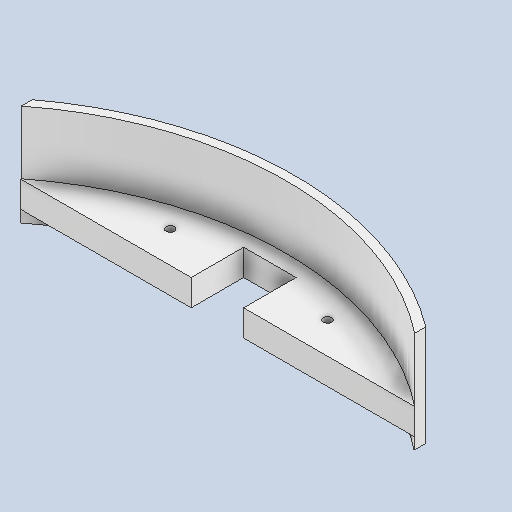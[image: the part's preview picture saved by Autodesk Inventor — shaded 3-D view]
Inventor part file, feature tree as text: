
AUTODESK INVENTOR PART (.ipt)
format: ipt  version: 2023 (Build 270158000, 158)  size: 375,296 bytes
history: native  units: mm
features: sketch x14, extrude x13, other x1, hole x1
ambient origin geometry x8: Origin, YZ Plane, XZ Plane, XY Plane, X Axis, Y Axis, Z Axis, Center Point
bodies: Body1 (feature_tree)
feature tree (29):
  other  "ソリッド1"
  extrude  "押し出し1"  Depth=250.0mm
  extrude  "押し出し2"  Depth=4.0mm TaperAngle=0.0deg
  sketch  "スケッチ4"
  extrude  "押し出し3"  Depth=150.0mm
  extrude  "押し出し4"  Depth=180.0mm
  extrude  "押し出し5"  Depth=243.0mm
  extrude  "押し出し6"  Depth=30.0mm TaperAngle=360.0deg
  extrude  "押し出し7"  Depth=10.0mm TaperAngle=0.0deg
  extrude  "押し出し8"  Depth=243.0mm
  extrude  "押し出し9"  Depth=243.0mm
  hole  "穴1"  [1 undecoded]
  extrude  "押し出し10"  Depth=30.0mm
  extrude  "押し出し11"  Depth=30.0mm
  extrude  "押し出し12"  Depth=10.0mm TaperAngle=0.0deg
  extrude  "押し出し13"  Depth=243.0mm
  sketch  "スケッチ1"
  sketch  "スケッチ2"
  sketch  "スケッチ5"
  sketch  "スケッチ6"
  sketch  "スケッチ7"
  sketch  "スケッチ8"
  sketch  "スケッチ9"
  sketch  "スケッチ12"
  sketch  "スケッチ13"
  sketch  "スケッチ14"
  sketch  "スケッチ15"
  sketch  "スケッチ16"
  sketch  "スケッチ17"
note: 1 required parameter value undecoded (feature->parameter linkage not recoverable at this tier; creation-order binding heuristic only, values carry confidence <= 0.55)
